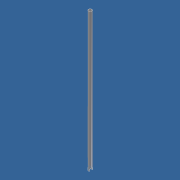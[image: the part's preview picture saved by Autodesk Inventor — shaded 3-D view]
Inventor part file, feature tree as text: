
AUTODESK INVENTOR PART (.ipt)
format: ipt  version: unknown  size: 176,128 bytes
history: native  units: mm
features: extrude x2, sketch x2, other x1
ambient origin geometry x7: Origin, YZ Plane, XZ Plane, X Axis, Y Axis, Z Axis, Center Point
bodies: Solido1 (feature_tree)
feature tree (5):
  extrude  "Estrusione1"  Depth=25.0mm
  extrude  "Estrusione2"  Depth=1.0mm
  other  "Piacno XY"
  sketch  "Schizzo1"
  sketch  "Schizzo2"
